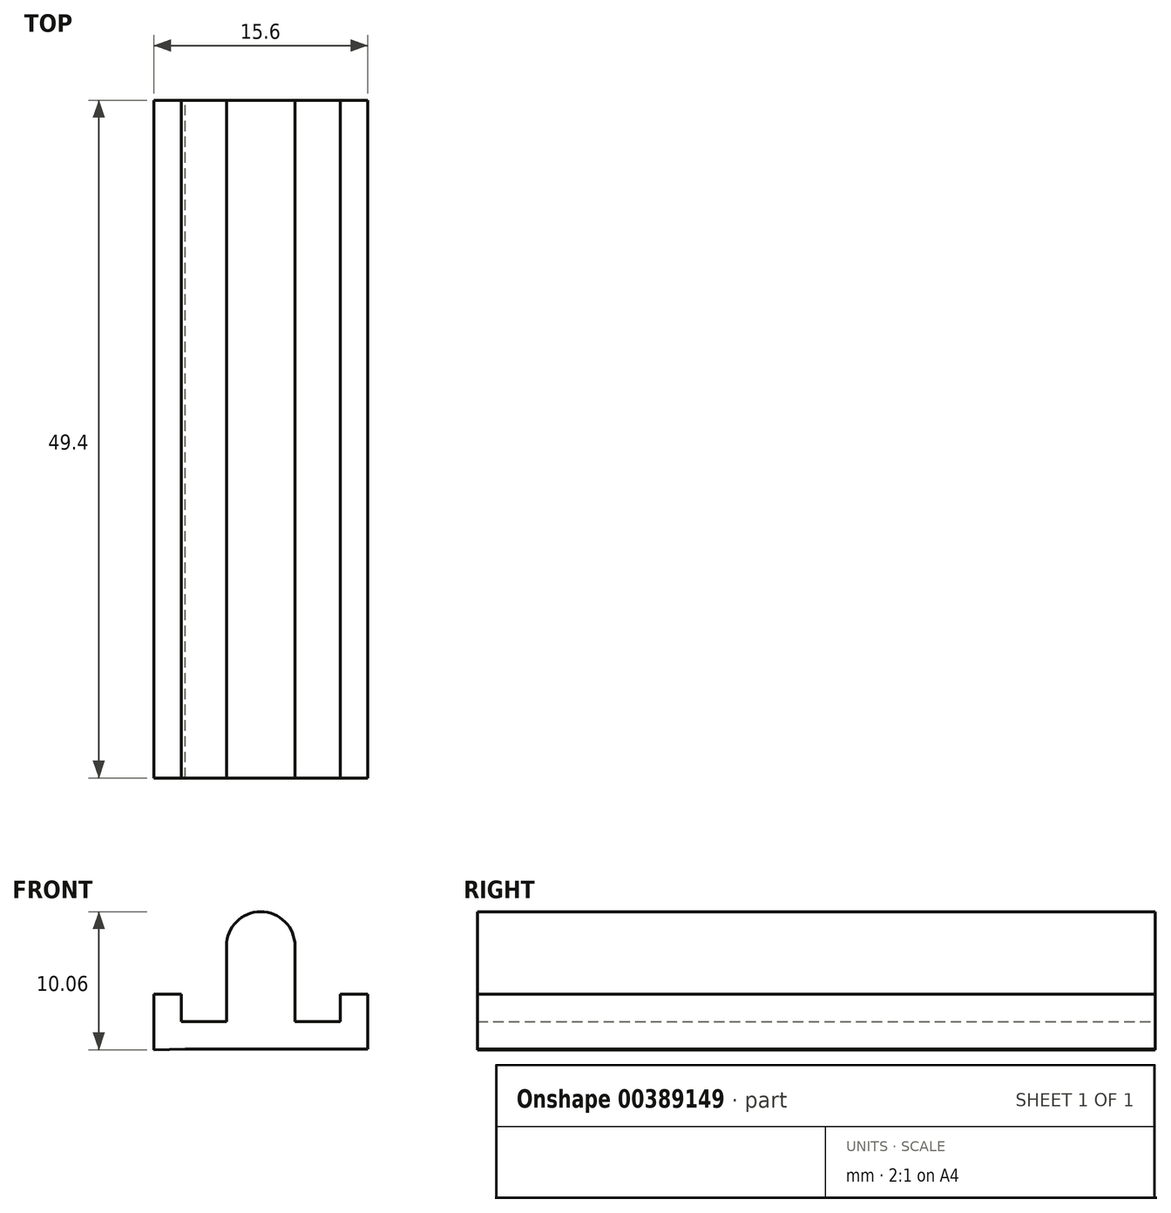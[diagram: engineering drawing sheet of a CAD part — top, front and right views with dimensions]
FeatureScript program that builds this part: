
annotation { "Feature Type Name" : "Feature", "Feature Type Description" : "" }
export const myFeature = defineFeature(function(context is Context, id is Id, definition is map)
    precondition{}
    {
        {
            var Q0;
            Q0=qCreatedBy(makeId("Front.planeOp"),FACE);
            var sketch = newSketch(context, id + "F0", { "sketchPlane" : qUnion([Q0])});
            skLineSegment(sketch, "E0", {"start": v(0, 0) * mm, "end": v(3, 0) * mm});
            skLineSegment(sketch, "E1", {"start": v(0, 0) * mm, "end": v(2, 0) * mm});
            skPoint(sketch, "E2.start.orphan", {"position": v(6, 4) * mm});
            skPoint(sketch, "E3.start.orphan", {"position": v(0, 8) * mm});
            skLineSegment(sketch, "E4", {"start": v(9, -2) * mm, "end": v(0, -2) * mm});
            skPoint(sketch, "E5.orphan", {"position": v(0, 0.6) * mm});
            skPoint(sketch, "E6.end.orphan", {"position": v(3.5, 4) * mm});
            skPoint(sketch, "E6.start.orphan", {"position": v(1, 4) * mm});
            skPoint(sketch, "E7.start.orphan", {"position": v(5, 4) * mm});
            skPoint(sketch, "E8.start.orphan", {"position": v(5, 0) * mm});
            skPoint(sketch, "E9.start.orphan", {"position": v(8, 0) * mm});
            skLineSegment(sketch, "E10", {"start": v(3, 0) * mm, "end": v(3, 5.5) * mm});
            skLineSegment(sketch, "E11", {"start": v(3, 5.5) * mm, "end": v(5.5, 5.5) * mm});
            skArc(sketch, "E12", {"start": v(3, 5.5) * mm, "mid": v(5.5, 8) * mm, "end": v(8, 5.5) * mm});
            skLineSegment(sketch, "E13", {"start": v(8, 5.5) * mm, "end": v(8, 0) * mm});
            skLineSegment(sketch, "E14", {"start": v(8, 0) * mm, "end": v(11, 0) * mm});
            skLineSegment(sketch, "E15", {"start": v(11, 0) * mm, "end": v(11.3, 0) * mm});
            skLineSegment(sketch, "E16", {"start": v(11.3, 0) * mm, "end": v(11.3, 2) * mm});
            skLineSegment(sketch, "E17", {"start": v(11.3, 2) * mm, "end": v(13.3, 2) * mm});
            skLineSegment(sketch, "E18", {"start": v(13.3, 2) * mm, "end": v(13.3, -2) * mm});
            skLineSegment(sketch, "E19", {"start": v(13.3, -2) * mm, "end": v(9, -2) * mm});
            skLineSegment(sketch, "E20", {"start": v(0, 0) * mm, "end": v(-0.3, 0) * mm});
            skLineSegment(sketch, "E21", {"start": v(-0.3, 0) * mm, "end": v(-0.3, 2) * mm});
            skLineSegment(sketch, "E22", {"start": v(-0.3, 2) * mm, "end": v(-2.3, 2) * mm});
            skLineSegment(sketch, "E23", {"start": v(-2.3, 2) * mm, "end": v(-2.3, -2.06) * mm});
            skLineSegment(sketch, "E24", {"start": v(-2.3, -2.06) * mm, "end": v(0, -2) * mm});
            skPoint(sketch, "E25.end.orphan", {"position": v(0, -1.4) * mm});
            skSolve(sketch);
        }
        {
            var Q0;
            Q0=qSketchRegion(id+"F0",true);
            extrude(context, id + "F1", {"entities" : qUnion([Q0]), "depth" : 49.4 * mm});
        }
    });
